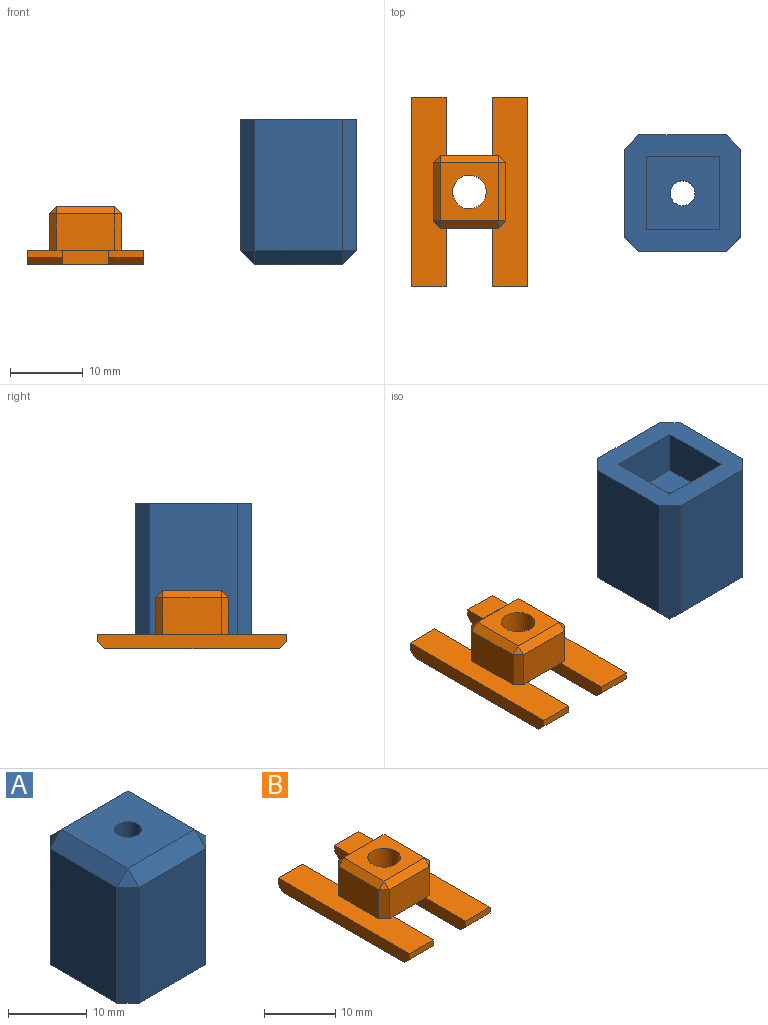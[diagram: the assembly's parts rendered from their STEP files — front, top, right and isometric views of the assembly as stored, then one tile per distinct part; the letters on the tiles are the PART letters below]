
ASSEMBLY  parts=2 mates=1
PART A: 24 faces, bbox 16x16x20 mm
  f0: plane 18x12mm, normal (0,-1,0), area 216mm2, adj f6,f14,f19,f20
  f1: plane 18x12mm, normal (1,0,0), area 216mm2, adj f6,f12,f13,f14
  f2: plane 18x12mm, normal (0,1,0), area 216mm2, adj f6,f12,f17,f18
  f3: plane 18x12mm, normal (-1,0,0), area 216mm2, adj f6,f17,f20,f23
  f4: cylinder r=1.7mm len=14mm, axis (0,0,-1), area 149.5mm2, adj f5,f11
  f5: plane 12x12mm, normal (0,0,1), area 134.9mm2, adj f4,f13,f18,f19,f23
  f6: plane 16x16mm, normal (0,0,-1), area 147.6mm2, adj f0,f1,f2,f3,f7,f8,f9,f10
  f7: plane 10.02x6mm, normal (0,-1,0), area 60.1mm2, adj f6,f8,f10,f11
  f8: plane 10.02x6mm, normal (1,0,0), area 60.1mm2, adj f6,f7,f9,f11
  f9: plane 10.02x6mm, normal (0,1,0), area 60.1mm2, adj f6,f8,f10,f11
  f10: plane 10.02x6mm, normal (-1,0,0), area 60.1mm2, adj f6,f7,f9,f11
  f11: plane 10.02x10.02mm, normal (0,0,-1), area 91.3mm2, adj f4,f7,f8,f9,f10
  f12: plane 18x2mm, normal (0.71,0.71,0), area 50.9mm2, adj f1,f2,f6,f15
  f13: plane 12x2mm, normal (0.71,0,0.71), area 33.9mm2, adj f1,f5,f15,f16
  f14: plane 18x2mm, normal (0.71,-0.71,0), area 50.9mm2, adj f0,f1,f6,f16
  f15: plane 2x2mm, normal (0.58,0.58,0.58), area 3.5mm2, adj f12,f13,f18
  f16: plane 2x2mm, normal (0.58,-0.58,0.58), area 3.5mm2, adj f13,f14,f19
  f17: plane 18x2mm, normal (-0.71,0.71,0), area 50.9mm2, adj f2,f3,f6,f21
  f18: plane 12x2mm, normal (0,0.71,0.71), area 33.9mm2, adj f2,f5,f15,f21
  f19: plane 12x2mm, normal (0,-0.71,0.71), area 33.9mm2, adj f0,f5,f16,f22
  f20: plane 18x2mm, normal (-0.71,-0.71,0), area 50.9mm2, adj f0,f3,f6,f22
  f21: plane 2x2mm, normal (-0.58,0.58,0.58), area 3.5mm2, adj f17,f18,f23
  f22: plane 2x2mm, normal (-0.58,-0.58,0.58), area 3.5mm2, adj f19,f20,f23
  f23: plane 12x2mm, normal (-0.71,0,0.71), area 33.9mm2, adj f3,f5,f21,f22
PART B: 39 faces, bbox 16x26x8 mm
  f0: plane 7.98x5mm, normal (0,-1,0), area 39.9mm2, adj f2,f15,f20,f26,f27,f36
  f1: plane 7.98x5mm, normal (0,1,0), area 39.9mm2, adj f2,f15,f19,f24,f25,f38
  f2: plane 26x4.8mm, normal (0,0,1), area 107.9mm2, adj f0,f1,f3,f9,f10,f11,f12,f17
  f3: plane 10x2mm, normal (1,0,0), area 19.5mm2, adj f2,f12,f14,f31,f35,f36
  f4: plane 10x2mm, normal (-1,0,0), area 19.5mm2, adj f5,f14,f15,f32,f35,f36
  f5: plane 4.8x1mm, normal (0,-1,0), area 4.8mm2, adj f4,f6,f15,f32
  f6: plane 26x2mm, normal (1,0,0), area 51mm2, adj f5,f7,f14,f15,f32,f33
  f7: plane 4.8x1mm, normal (0,1,0), area 4.8mm2, adj f6,f8,f15,f33
  f8: plane 9.99x2mm, normal (-1,0,0), area 19.5mm2, adj f7,f14,f15,f33,f37,f38
  f9: plane 9.99x2mm, normal (1,0,0), area 19.5mm2, adj f2,f10,f14,f34,f37,f38
  f10: plane 4.8x1mm, normal (0,1,0), area 4.8mm2, adj f2,f9,f11,f34
  f11: plane 26x2mm, normal (-1,0,0), area 51mm2, adj f2,f10,f12,f14,f31,f34
  f12: plane 4.8x1mm, normal (0,-1,0), area 4.8mm2, adj f2,f3,f11,f31
  f13: cylinder r=2.3mm len=8mm, axis (0,0,1), area 115.6mm2, adj f14,f18
  f14: plane 24x16mm, normal (0,0,-1), area 252.2mm2, adj f3,f4,f6,f8,f9,f11,f13,f31
  f15: plane 26x4.8mm, normal (0,0,1), area 107.9mm2, adj f0,f1,f4,f5,f6,f7,f8,f16
  f16: plane 7.98x5mm, normal (1,0,0), area 39.9mm2, adj f15,f25,f26,f30
  f17: plane 7.98x5mm, normal (-1,0,0), area 39.9mm2, adj f2,f19,f20,f21
  f18: plane 7.98x7.98mm, normal (0,0,1), area 47.1mm2, adj f13,f21,f24,f27,f30
  f19: plane 5x1mm, normal (-0.71,0.71,0), area 7.1mm2, adj f1,f2,f17,f22
  f20: plane 5x1mm, normal (-0.71,-0.71,0), area 7.1mm2, adj f0,f2,f17,f23
  f21: plane 7.98x1mm, normal (-0.71,0,0.71), area 11.3mm2, adj f17,f18,f22,f23
  f22: plane 1x1mm, normal (-0.58,0.58,0.58), area 0.9mm2, adj f19,f21,f24
  f23: plane 1x1mm, normal (-0.58,-0.58,0.58), area 0.9mm2, adj f20,f21,f27
  f24: plane 7.98x1mm, normal (0,0.71,0.71), area 11.3mm2, adj f1,f18,f22,f28
  f25: plane 5x1mm, normal (0.71,0.71,0), area 7.1mm2, adj f1,f15,f16,f28
  f26: plane 5x1mm, normal (0.71,-0.71,0), area 7.1mm2, adj f0,f15,f16,f29
  f27: plane 7.98x1mm, normal (0,-0.71,0.71), area 11.3mm2, adj f0,f18,f23,f29
  f28: plane 1x1mm, normal (0.58,0.58,0.58), area 0.9mm2, adj f24,f25,f30
  f29: plane 1x1mm, normal (0.58,-0.58,0.58), area 0.9mm2, adj f26,f27,f30
  f30: plane 7.98x1mm, normal (0.71,0,0.71), area 11.3mm2, adj f16,f18,f28,f29
  f31: plane 4.8x1mm, normal (0,-0.71,-0.71), area 6.8mm2, adj f3,f11,f12,f14
  f32: plane 4.8x1mm, normal (0,-0.71,-0.71), area 6.8mm2, adj f4,f5,f6,f14
  f33: plane 4.8x1mm, normal (0,0.71,-0.71), area 6.8mm2, adj f6,f7,f8,f14
  f34: plane 4.8x1mm, normal (0,0.71,-0.71), area 6.8mm2, adj f9,f10,f11,f14
  f35: plane 6.4x2mm, normal (0,-1,0), area 12.8mm2, adj f3,f4,f14,f36
  f36: plane 6.4x1.99mm, normal (0,0,-1), area 12.7mm2, adj f0,f3,f4,f35
  f37: plane 6.4x2mm, normal (0,1,0), area 12.8mm2, adj f8,f9,f14,f38
  f38: plane 6.4x1.98mm, normal (0,0,-1), area 12.7mm2, adj f1,f8,f9,f37
PLACE A rot(axis=(-1,0,0),180deg) t=(14.3,-0.15,33.64)mm
PLACE B t=(-14.96,0.03,-0.36)mm
MATE planar B.f13 <-> A.f4  axis (0,0,-1) through (-14.96,0.04,-2.36)mm
